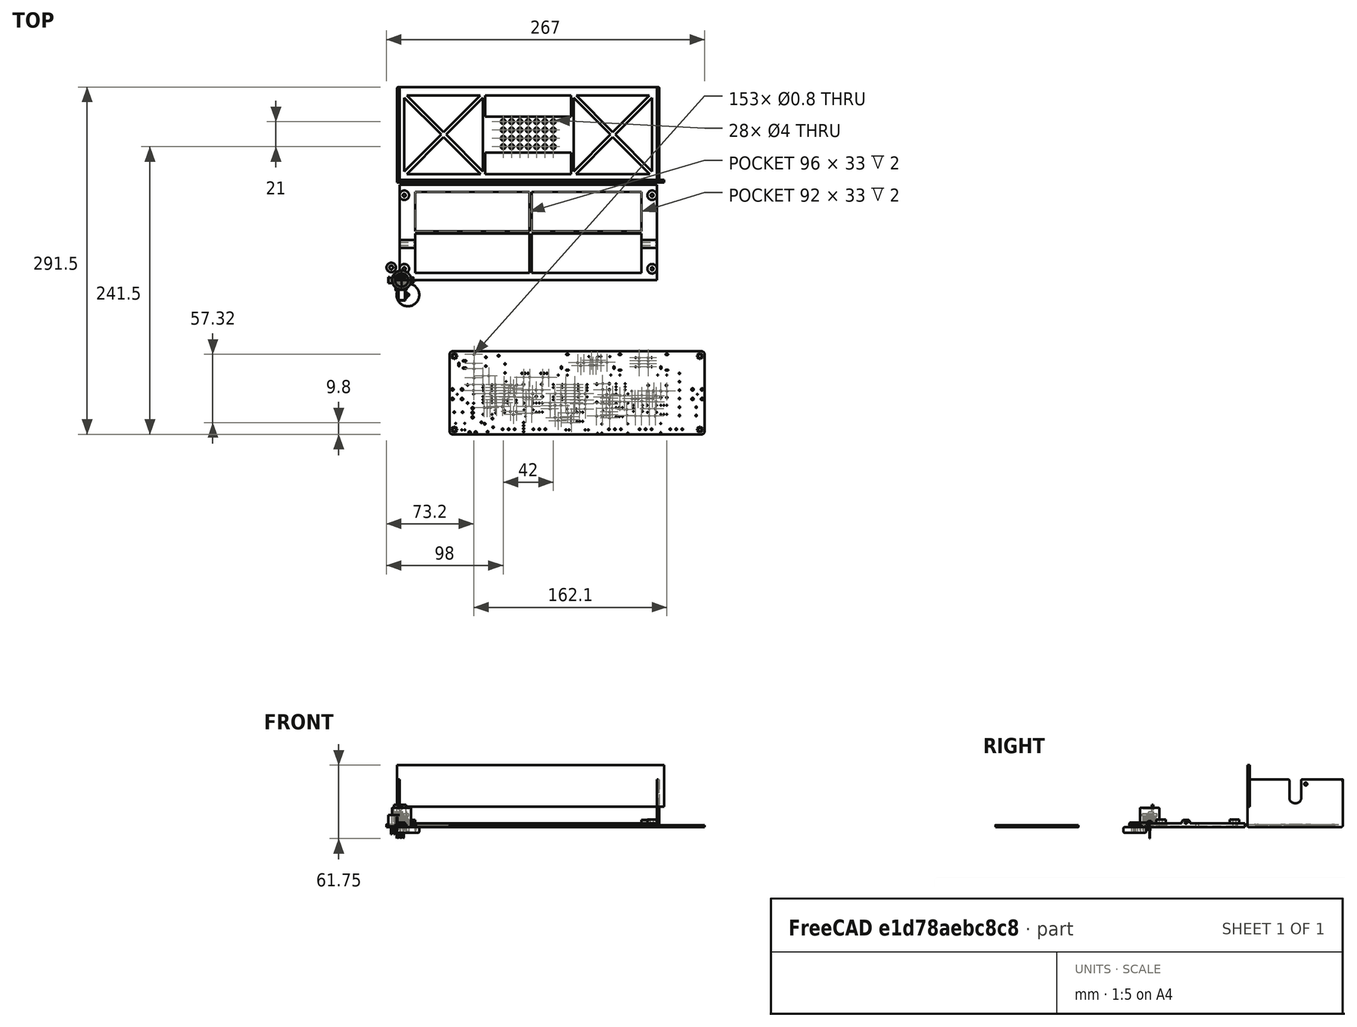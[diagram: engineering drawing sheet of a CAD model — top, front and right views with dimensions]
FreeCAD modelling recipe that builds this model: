
FCSTD DOCUMENT  (FreeCAD 0.18R16110 (Git))
Label: theresynth-case
License: All rights reserved
LicenseURL: http://en.wikipedia.org/wiki/All_rights_reserved
objects: Part::Feature×127, App::Part×126, Part::Cylinder×43, Part::Box×18, Part::MultiFuse×7, Part::Cut×6, Part::Fillet×5, Mesh::Feature×5
note: 206 computed .brp shape members not serialized (recipe doc carries the construction recipe); baked Part::Feature solids carry a one-line shape summary decoded from their .brp

FEATURE [Part::Box] Box  label="Base"
  AttacherType = Attacher::AttachEngine3D
  Height = 3
  Length = 216
  Placement = pos=(2,0,0) rot=(0,0,1;0rad)
  Width = 80
FEATURE [Part::Cylinder] Cylinder  label="ScrewHole"
  Angle = 360
  AttacherType = Attacher::AttachEngine3D
  Height = 7
  Placement = pos=(6,9.5,0) rot=(0,0,1;0rad)
  Radius = 1.25
FEATURE [Part::Feature] Part__Feature  label="SOLID"
  shape: bbox 19.77 x 20.45 x 18 mm, 56 faces (baked)
FEATURE [App::Part] CP_Radial_D16_0mm_P7_50mm  label="CP_Radial_D16.0mm_P7.50mm"
  Group = -> [Part__Feature]
  Origin = -> Origin
  Placement = pos=(74.42,-72.22,1.65) rot=(0,0,1;1.5708rad)
FEATURE [Part::Feature] Part__Feature001  label="SOLID001"
  shape: bbox 19.77 x 20.45 x 18 mm, 56 faces (baked)
FEATURE [App::Part] CP_Radial_D16_0mm_P7_50mm001  label="CP_Radial_D16.0mm_P7.50mm001"
  Group = -> [Part__Feature001]
  Origin = -> Origin001
  Placement = pos=(90.52,-70.42,1.65) rot=(0,0,-1;1.5708rad)
FEATURE [Part::Feature] Part__Feature002  label="SOLID002"
  shape: bbox 8.285 x 1.732 x 4.666 mm, 17 faces (baked)
FEATURE [App::Part] R_Axial_DIN0204_L3_6mm_D1_6mm_P7_62mm_Horizontal  label="R_Axial_DIN0204_L3.6mm_D1.6mm_P7.62mm_Horizontal"
  Group = -> [Part__Feature002]
  Origin = -> Origin002
  Placement = pos=(82.5,-111.57,1.65) rot=(0,0,1;0rad)
FEATURE [Part::Feature] Part__Feature003  label="SOLID003"
  shape: bbox 8.306 x 1.61 x 4.605 mm, 21 faces (baked)
FEATURE [App::Part] D_DO_34_SOD68_P7_62mm_Horizontal  label="D_DO-34_SOD68_P7.62mm_Horizontal"
  Group = -> [Part__Feature003]
  Origin = -> Origin003
  Placement = pos=(90.1,-109.17,1.65) rot=(0,0,1;3.14159rad)
FEATURE [Part::Feature] Part__Feature004  label="SOLID004"
  shape: bbox 8.306 x 1.61 x 4.605 mm, 21 faces (baked)
FEATURE [App::Part] D_DO_34_SOD68_P7_62mm_Horizontal001  label="D_DO-34_SOD68_P7.62mm_Horizontal001"
  Group = -> [Part__Feature004]
  Origin = -> Origin004
  Placement = pos=(64.2,-95.7,1.65) rot=(0,0,-1;1.5708rad)
FEATURE [Part::Feature] Part__Feature005  label="SOLID005"
  shape: bbox 8.306 x 1.61 x 4.605 mm, 21 faces (baked)
FEATURE [App::Part] D_DO_34_SOD68_P7_62mm_Horizontal002  label="D_DO-34_SOD68_P7.62mm_Horizontal002"
  Group = -> [Part__Feature005]
  Origin = -> Origin005
  Placement = pos=(178.49,-64.2,1.65) rot=(0,0,1;3.14159rad)
FEATURE [Part::Feature] Part__Feature006  label="SOLID006"
  shape: bbox 2.54 x 10.16 x 11.54 mm, 100 faces (baked)
FEATURE [App::Part] PinHeader_1x04_P2_54mm_Vertical  label="PinHeader_1x04_P2.54mm_Vertical"
  Group = -> [Part__Feature006]
  Origin = -> Origin006
  Placement = pos=(106.2,-127.27,1.65) rot=(0,0,1;3.14159rad)
FEATURE [Part::Feature] Part__Feature007  label="SOLID007"
  shape: bbox 8.285 x 1.732 x 4.666 mm, 17 faces (baked)
FEATURE [App::Part] R_Axial_DIN0204_L3_6mm_D1_6mm_P7_62mm_Horizontal001  label="R_Axial_DIN0204_L3.6mm_D1.6mm_P7.62mm_Horizontal001"
  Group = -> [Part__Feature007]
  Origin = -> Origin007
  Placement = pos=(221.2,-120.47,1.65) rot=(0,0,-1;1.5708rad)
FEATURE [Part::Feature] Part__Feature008  label="SOLID008"
  shape: bbox 8.285 x 1.732 x 4.666 mm, 17 faces (baked)
FEATURE [App::Part] R_Axial_DIN0204_L3_6mm_D1_6mm_P7_62mm_Horizontal002  label="R_Axial_DIN0204_L3.6mm_D1.6mm_P7.62mm_Horizontal002"
  Group = -> [Part__Feature008]
  Origin = -> Origin008
  Placement = pos=(200.1,-72.77,1.65) rot=(0,0,1;1.5708rad)
FEATURE [Part::Feature] Part__Feature009  label="SOLID009"
  shape: bbox 7.874 x 9.27 x 6.98 mm, 148 faces (baked)
FEATURE [App::Part] DIP_8_W7_62mm  label="DIP-8_W7.62mm"
  Group = -> [Part__Feature009]
  Origin = -> Origin009
  Placement = pos=(203,-65.17,1.65) rot=(0,0,1;0rad)
FEATURE [Part::Feature] Part__Feature010  label="SOLID010"
  shape: bbox 7.874 x 19.05 x 6.98 mm, 250 faces (baked)
FEATURE [App::Part] DIP_14_W7_62mm  label="DIP-14_W7.62mm"
  Group = -> [Part__Feature010]
  Origin = -> Origin010
  Placement = pos=(141.46,-87.66,1.65) rot=(0,0,1;0rad)
FEATURE [Part::Feature] Part__Feature011  label="SOLID011"
  shape: bbox 8.285 x 1.732 x 4.666 mm, 17 faces (baked)
FEATURE [App::Part] R_Axial_DIN0204_L3_6mm_D1_6mm_P7_62mm_Horizontal003  label="R_Axial_DIN0204_L3.6mm_D1.6mm_P7.62mm_Horizontal003"
  Group = -> [Part__Feature011]
  Origin = -> Origin011
  Placement = pos=(72.01,-92.65,1.65) rot=(0,0,1;0rad)
FEATURE [Part::Feature] Part__Feature012  label="SOLID012"
  shape: bbox 7 x 6 x 11.9 mm, 22 faces (baked)
FEATURE [App::Part] C_Rect_L7_0mm_W6_0mm_P5_00mm  label="C_Rect_L7.0mm_W6.0mm_P5.00mm"
  Group = -> [Part__Feature012]
  Origin = -> Origin012
  Placement = pos=(172.3,-114.14,1.65) rot=(0,0,1;3.14159rad)
FEATURE [Part::Feature] Part__Feature013  label="SOLID013"
  shape: bbox 8.285 x 1.732 x 4.666 mm, 17 faces (baked)
FEATURE [App::Part] R_Axial_DIN0204_L3_6mm_D1_6mm_P7_62mm_Horizontal004  label="R_Axial_DIN0204_L3.6mm_D1.6mm_P7.62mm_Horizontal004"
  Group = -> [Part__Feature013]
  Origin = -> Origin013
  Placement = pos=(72.02,-87.86,1.65) rot=(0,0,1;0rad)
FEATURE [Part::Feature] Part__Feature014  label="SOLID014"
  shape: bbox 8.285 x 1.732 x 4.666 mm, 17 faces (baked)
FEATURE [App::Part] R_Axial_DIN0204_L3_6mm_D1_6mm_P7_62mm_Horizontal005  label="R_Axial_DIN0204_L3.6mm_D1.6mm_P7.62mm_Horizontal005"
  Group = -> [Part__Feature014]
  Origin = -> Origin014
  Placement = pos=(79.64,-90.245,1.65) rot=(0,0,1;3.14159rad)
FEATURE [Part::Feature] Part__Feature015  label="SOLID015"
  shape: bbox 8.285 x 1.732 x 4.666 mm, 17 faces (baked)
FEATURE [App::Part] R_Axial_DIN0204_L3_6mm_D1_6mm_P7_62mm_Horizontal006  label="R_Axial_DIN0204_L3.6mm_D1.6mm_P7.62mm_Horizontal006"
  Group = -> [Part__Feature015]
  Origin = -> Origin015
  Placement = pos=(193.68,-103.2,1.65) rot=(0,0,1;1.5708rad)
FEATURE [Part::Feature] Part__Feature016  label="SOLID016"
  shape: bbox 6 x 2.5 x 8.1 mm, 12 faces (baked)
FEATURE [App::Part] C_Disc_D6_0mm_W2_5mm_P5_00mm  label="C_Disc_D6.0mm_W2.5mm_P5.00mm"
  Group = -> [Part__Feature016]
  Origin = -> Origin016
  Placement = pos=(172.4,-91.94,1.65) rot=(0,0,1;1.5708rad)
FEATURE [Part::Feature] Part__Feature017  label="SOLID017"
  shape: bbox 7.874 x 19.05 x 6.98 mm, 250 faces (baked)
FEATURE [App::Part] DIP_14_W7_62mm001  label="DIP-14_W7.62mm001"
  Group = -> [Part__Feature017]
  Origin = -> Origin017
  Placement = pos=(82.21,-87.7,1.65) rot=(0,0,1;0rad)
FEATURE [Part::Feature] Part__Feature018  label="SOLID018"
  shape: bbox 8.285 x 1.732 x 4.666 mm, 17 faces (baked)
FEATURE [App::Part] R_Axial_DIN0204_L3_6mm_D1_6mm_P7_62mm_Horizontal007  label="R_Axial_DIN0204_L3.6mm_D1.6mm_P7.62mm_Horizontal007"
  Group = -> [Part__Feature018]
  Origin = -> Origin018
  Placement = pos=(72,-112.77,1.65) rot=(0,0,1;0rad)
FEATURE [Part::Feature] Part__Feature019  label="SOLID019"
  shape: bbox 10.25 x 4.455 x 28.53 mm, 48 faces (baked)
FEATURE [App::Part] TO_220_3_Vertical  label="TO-220-3_Vertical"
  Group = -> [Part__Feature019]
  Origin = -> Origin019
  Placement = pos=(104.83,-78.28,1.65) rot=(0,0,1;0rad)
FEATURE [Part::Feature] Part__Feature020  label="SOLID020"
  shape: bbox 10.25 x 4.455 x 28.53 mm, 48 faces (baked)
FEATURE [App::Part] TO_220_3_Vertical001  label="TO-220-3_Vertical001"
  Group = -> [Part__Feature020]
  Origin = -> Origin020
  Placement = pos=(120.77,-78.28,1.65) rot=(0,0,1;0rad)
FEATURE [Part::Feature] Part__Feature021  label="SOLID021"
  shape: bbox 2.8 x 0.6 x 8.5 mm, 15 faces (baked)
FEATURE [App::Part] Pin_D1_4mm_L8_5mm_W2_8mm_FlatFork  label="Pin_D1.4mm_L8.5mm_W2.8mm_FlatFork"
  Group = -> [Part__Feature021]
  Origin = -> Origin021
  Placement = pos=(85.16,-63.49,1.65) rot=(0,0,1;0rad)
FEATURE [Part::Feature] Part__Feature022  label="SOLID022"
  shape: bbox 8.285 x 1.732 x 4.666 mm, 17 faces (baked)
FEATURE [App::Part] R_Axial_DIN0204_L3_6mm_D1_6mm_P7_62mm_Horizontal008  label="R_Axial_DIN0204_L3.6mm_D1.6mm_P7.62mm_Horizontal008"
  Group = -> [Part__Feature022]
  Origin = -> Origin022
  Placement = pos=(56.7,-120.2,1.65) rot=(0,0,1;3.14159rad)
FEATURE [Part::Feature] Part__Feature023  label="SOLID023"
  shape: bbox 3.4 x 3.8 x 10.8 mm, 16 faces (baked)
FEATURE [App::Part] LED_D3_0mm  label="LED_D3.0mm"
  Group = -> [Part__Feature023]
  Origin = -> Origin023
  Placement = pos=(54.2,-125.75,1.65) rot=(0,0,1;0rad)
FEATURE [Part::Feature] Part__Feature024  label="SOLID024"
  shape: bbox 8.285 x 1.732 x 4.666 mm, 17 faces (baked)
FEATURE [App::Part] R_Axial_DIN0204_L3_6mm_D1_6mm_P7_62mm_Horizontal009  label="R_Axial_DIN0204_L3.6mm_D1.6mm_P7.62mm_Horizontal009"
  Group = -> [Part__Feature024]
  Origin = -> Origin024
  Placement = pos=(138.72,-87.64,1.65) rot=(0,0,1;3.14159rad)
FEATURE [Part::Feature] Part__Feature025  label="SOLID025"
  shape: bbox 8.285 x 1.732 x 4.666 mm, 17 faces (baked)
FEATURE [App::Part] R_Axial_DIN0204_L3_6mm_D1_6mm_P7_62mm_Horizontal010  label="R_Axial_DIN0204_L3.6mm_D1.6mm_P7.62mm_Horizontal010"
  Group = -> [Part__Feature025]
  Origin = -> Origin025
  Placement = pos=(159.43,-87.72,1.65) rot=(0,0,1;3.14159rad)
FEATURE [Part::Feature] Part__Feature026  label="SOLID026"
  shape: bbox 9.53 x 4.83 x 17.07 mm, 32 faces (baked)
FEATURE [App::Part] Potentiometer_Bourns_3296W_Vertical
  Group = -> [Part__Feature026]
  Origin = -> Origin026
  Placement = pos=(161.84,-71.6,1.65) rot=(0,0,1;3.14159rad)
FEATURE [Part::Feature] Part__Feature027  label="SOLID027"
  shape: bbox 8.285 x 1.732 x 4.666 mm, 17 faces (baked)
FEATURE [App::Part] R_Axial_DIN0204_L3_6mm_D1_6mm_P7_62mm_Horizontal011  label="R_Axial_DIN0204_L3.6mm_D1.6mm_P7.62mm_Horizontal011"
  Group = -> [Part__Feature027]
  Origin = -> Origin027
  Placement = pos=(213.6,-72.77,1.65) rot=(0,0,1;1.5708rad)
FEATURE [Part::Feature] Part__Feature028  label="SOLID028"
  shape: bbox 3.4 x 3.8 x 10.8 mm, 16 faces (baked)
FEATURE [App::Part] LED_D3_0mm001  label="LED_D3.0mm001"
  Group = -> [Part__Feature028]
  Origin = -> Origin028
  Placement = pos=(157.84,-125.75,1.65) rot=(0,0,1;0rad)
FEATURE [Part::Feature] Part__Feature029  label="SOLID029"
  shape: bbox 9.53 x 4.83 x 17.07 mm, 32 faces (baked)
FEATURE [App::Part] Potentiometer_Bourns_3296W_Vertical001
  Group = -> [Part__Feature029]
  Origin = -> Origin029
  Placement = pos=(78.1,-107,1.65) rot=(0,0,1;0rad)
FEATURE [Part::Feature] Part__Feature030  label="SOLID030"
  shape: bbox 7.2 x 2.5 x 10.9 mm, 22 faces (baked)
FEATURE [App::Part] C_Rect_L7_2mm_W2_5mm_P5_00mm_FKS2_FKP2_MKS2_MKP2  label="C_Rect_L7.2mm_W2.5mm_P5.00mm_FKS2_FKP2_MKS2_MKP2"
  Group = -> [Part__Feature030]
  Origin = -> Origin030
  Placement = pos=(93.6,-94.9,1.65) rot=(0,0,1;0rad)
FEATURE [Part::Feature] Part__Feature031  label="SOLID031"
  shape: bbox 7.2 x 2.5 x 10.9 mm, 22 faces (baked)
FEATURE [App::Part] C_Rect_L7_2mm_W2_5mm_P5_00mm_FKS2_FKP2_MKS2_MKP2001  label="C_Rect_L7.2mm_W2.5mm_P5.00mm_FKS2_FKP2_MKS2_MKP003"
  Group = -> [Part__Feature031]
  Origin = -> Origin031
  Placement = pos=(78.2,-95.3,1.65) rot=(0,0,1;3.14159rad)
FEATURE [Part::Feature] Part__Feature032  label="SOLID032"
  shape: bbox 7.2 x 2.5 x 10.9 mm, 22 faces (baked)
FEATURE [App::Part] C_Rect_L7_2mm_W2_5mm_P5_00mm_FKS2_FKP2_MKS2_MKP2002  label="C_Rect_L7.2mm_W2.5mm_P5.00mm_FKS2_FKP2_MKS2_MKP004"
  Group = -> [Part__Feature032]
  Origin = -> Origin032
  Placement = pos=(152.9,-95.4,1.65) rot=(0,0,1;0rad)
FEATURE [Part::Feature] Part__Feature033  label="SOLID033"
  shape: bbox 7.2 x 2.5 x 10.9 mm, 22 faces (baked)
FEATURE [App::Part] C_Rect_L7_2mm_W2_5mm_P5_00mm_FKS2_FKP2_MKS2_MKP2003  label="C_Rect_L7.2mm_W2.5mm_P5.00mm_FKS2_FKP2_MKS2_MKP005"
  Group = -> [Part__Feature033]
  Origin = -> Origin033
  Placement = pos=(137.4,-95.3,1.65) rot=(0,0,1;3.14159rad)
FEATURE [Part::Feature] Part__Feature034  label="SOLID034"
  shape: bbox 7.2 x 2.5 x 10.9 mm, 22 faces (baked)
FEATURE [App::Part] C_Rect_L7_2mm_W2_5mm_P5_00mm_FKS2_FKP2_MKS2_MKP2004  label="C_Rect_L7.2mm_W2.5mm_P5.00mm_FKS2_FKP2_MKS2_MKP006"
  Group = -> [Part__Feature034]
  Origin = -> Origin034
  Placement = pos=(180.9,-96.1,1.65) rot=(0,0,1;3.14159rad)
FEATURE [Part::Feature] Part__Feature035  label="SOLID035"
  shape: bbox 7.2 x 2.5 x 10.9 mm, 22 faces (baked)
FEATURE [App::Part] C_Rect_L7_2mm_W2_5mm_P5_00mm_FKS2_FKP2_MKS2_MKP2005  label="C_Rect_L7.2mm_W2.5mm_P5.00mm_FKS2_FKP2_MKS2_MKP007"
  Group = -> [Part__Feature035]
  Origin = -> Origin035
  Placement = pos=(217.2,-102.1,1.65) rot=(0,0,1;1.5708rad)
FEATURE [Part::Feature] Part__Feature036  label="COMPOUND"
  shape: bbox 8.244 x 2.165 x 5.082 mm, 16 faces, 2 solids (baked)
FEATURE [App::Part] D_DO_35_SOD27_P7_62mm_Horizontal  label="D_DO-35_SOD27_P7.62mm_Horizontal"
  Group = -> [Part__Feature036]
  Origin = -> Origin036
  Placement = pos=(64.5,-70,1.65) rot=(0,0,1;1.5708rad)
FEATURE [Part::Feature] Part__Feature037  label="COMPOUND001"
  shape: bbox 8.244 x 2.165 x 5.082 mm, 16 faces, 2 solids (baked)
FEATURE [App::Part] D_DO_35_SOD27_P7_62mm_Horizontal001  label="D_DO-35_SOD27_P7.62mm_Horizontal001"
  Group = -> [Part__Feature037]
  Origin = -> Origin037
  Placement = pos=(64.45,-82.05,1.65) rot=(0,0,1;1.5708rad)
FEATURE [Part::Feature] Part__Feature038  label="SOLID036"
  shape: bbox 8.285 x 1.732 x 4.666 mm, 17 faces (baked)
FEATURE [App::Part] R_Axial_DIN0204_L3_6mm_D1_6mm_P7_62mm_Horizontal012  label="R_Axial_DIN0204_L3.6mm_D1.6mm_P7.62mm_Horizontal012"
  Group = -> [Part__Feature038]
  Origin = -> Origin038
  Placement = pos=(92.4,-100.75,1.65) rot=(0,0,1;0rad)
FEATURE [Part::Feature] Part__Feature039  label="SOLID037"
  shape: bbox 8.285 x 1.732 x 4.666 mm, 17 faces (baked)
FEATURE [App::Part] R_Axial_DIN0204_L3_6mm_D1_6mm_P7_62mm_Horizontal013  label="R_Axial_DIN0204_L3.6mm_D1.6mm_P7.62mm_Horizontal013"
  Group = -> [Part__Feature039]
  Origin = -> Origin039
  Placement = pos=(226.3,-79.77,1.65) rot=(0,0,1;3.14159rad)
FEATURE [Part::Feature] Part__Feature040  label="SOLID038"
  shape: bbox 8.285 x 1.732 x 4.666 mm, 17 faces (baked)
FEATURE [App::Part] R_Axial_DIN0204_L3_6mm_D1_6mm_P7_62mm_Horizontal014  label="R_Axial_DIN0204_L3.6mm_D1.6mm_P7.62mm_Horizontal014"
  Group = -> [Part__Feature040]
  Origin = -> Origin040
  Placement = pos=(186.94,-79.77,1.65) rot=(0,0,1;3.14159rad)
FEATURE [Part::Feature] Part__Feature041  label="SOLID039"
  shape: bbox 8.285 x 1.732 x 4.666 mm, 17 faces (baked)
FEATURE [App::Part] R_Axial_DIN0204_L3_6mm_D1_6mm_P7_62mm_Horizontal015  label="R_Axial_DIN0204_L3.6mm_D1.6mm_P7.62mm_Horizontal015"
  Group = -> [Part__Feature041]
  Origin = -> Origin041
  Placement = pos=(151.79,-90.22,1.65) rot=(0,0,1;0rad)
FEATURE [Part::Feature] Part__Feature042  label="SOLID040"
  shape: bbox 8.285 x 1.732 x 4.666 mm, 17 faces (baked)
FEATURE [App::Part] R_Axial_DIN0204_L3_6mm_D1_6mm_P7_62mm_Horizontal016  label="R_Axial_DIN0204_L3.6mm_D1.6mm_P7.62mm_Horizontal016"
  Group = -> [Part__Feature042]
  Origin = -> Origin042
  Placement = pos=(151.8,-98.1,1.65) rot=(0,0,1;0rad)
FEATURE [Part::Feature] Part__Feature043  label="SOLID041"
  shape: bbox 8.285 x 1.732 x 4.666 mm, 17 faces (baked)
FEATURE [App::Part] R_Axial_DIN0204_L3_6mm_D1_6mm_P7_62mm_Horizontal017  label="R_Axial_DIN0204_L3.6mm_D1.6mm_P7.62mm_Horizontal017"
  Group = -> [Part__Feature043]
  Origin = -> Origin043
  Placement = pos=(168.49,-64.2,1.65) rot=(0,0,1;3.14159rad)
FEATURE [Part::Feature] Part__Feature044  label="SOLID042"
  shape: bbox 8.285 x 1.732 x 4.666 mm, 17 faces (baked)
FEATURE [App::Part] R_Axial_DIN0204_L3_6mm_D1_6mm_P7_62mm_Horizontal018  label="R_Axial_DIN0204_L3.6mm_D1.6mm_P7.62mm_Horizontal018"
  Group = -> [Part__Feature044]
  Origin = -> Origin044
  Placement = pos=(159.4,-92.7,1.65) rot=(0,0,1;3.14159rad)
FEATURE [Part::Feature] Part__Feature045  label="SOLID043"
  shape: bbox 7.2 x 2.5 x 10.9 mm, 22 faces (baked)
FEATURE [App::Part] C_Rect_L7_2mm_W2_5mm_P5_00mm_FKS2_FKP2_MKS2_MKP2006  label="C_Rect_L7.2mm_W2.5mm_P5.00mm_FKS2_FKP2_MKS2_MKP008"
  Group = -> [Part__Feature045]
  Origin = -> Origin045
  Placement = pos=(152.9,-103.9,1.65) rot=(0,0,1;0rad)
FEATURE [Part::Feature] Part__Feature046  label="SOLID044"
  shape: bbox 7 x 6 x 11.9 mm, 22 faces (baked)
FEATURE [App::Part] C_Rect_L7_0mm_W6_0mm_P5_00mm001  label="C_Rect_L7.0mm_W6.0mm_P5.00mm001"
  Group = -> [Part__Feature046]
  Origin = -> Origin046
  Placement = pos=(176.09,-69,1.65) rot=(0,0,1;3.14159rad)
FEATURE [Part::Feature] Part__Feature047  label="SOLID045"
  shape: bbox 7.2 x 2.5 x 10.9 mm, 22 faces (baked)
FEATURE [App::Part] C_Rect_L7_2mm_W2_5mm_P5_00mm_FKS2_FKP2_MKS2_MKP2007  label="C_Rect_L7.2mm_W2.5mm_P5.00mm_FKS2_FKP2_MKS2_MKP009"
  Group = -> [Part__Feature047]
  Origin = -> Origin047
  Placement = pos=(152.9,-100.8,1.65) rot=(0,0,1;0rad)
FEATURE [Part::Feature] Part__Feature048  label="SOLID046"
  shape: bbox 7.2 x 2.5 x 10.9 mm, 22 faces (baked)
FEATURE [App::Part] C_Rect_L7_2mm_W2_5mm_P5_00mm_FKS2_FKP2_MKS2_MKP2008  label="C_Rect_L7.2mm_W2.5mm_P5.00mm_FKS2_FKP2_MKS2_MKP010"
  Group = -> [Part__Feature048]
  Origin = -> Origin048
  Placement = pos=(168.07,-67.22,1.65) rot=(0,0,1;3.14159rad)
FEATURE [Part::Feature] Part__Feature049  label="SOLID047"
  shape: bbox 5.58 x 3.745 x 10 mm, 27 faces (baked)
FEATURE [App::Part] TO_92_Inline_Wide  label="TO-92_Inline_Wide"
  Group = -> [Part__Feature049]
  Origin = -> Origin049
  Placement = pos=(105.7,-98.4,1.65) rot=(0,0,1;0rad)
FEATURE [Part::Feature] Part__Feature050  label="SOLID048"
  shape: bbox 5.58 x 3.745 x 10 mm, 27 faces (baked)
FEATURE [App::Part] TO_92_Inline_Wide001  label="TO-92_Inline_Wide001"
  Group = -> [Part__Feature050]
  Origin = -> Origin050
  Placement = pos=(128.4,-108.1,1.65) rot=(0,0,1;1.5708rad)
FEATURE [Part::Feature] Part__Feature051  label="SOLID049"
  shape: bbox 5.58 x 3.745 x 10 mm, 27 faces (baked)
FEATURE [App::Part] TO_92_Inline_Wide002  label="TO-92_Inline_Wide002"
  Group = -> [Part__Feature051]
  Origin = -> Origin051
  Placement = pos=(146.1,-119.7,1.65) rot=(0,0,1;1.5708rad)
FEATURE [Part::Feature] Part__Feature052  label="SOLID050"
  shape: bbox 5.58 x 3.745 x 10 mm, 27 faces (baked)
FEATURE [App::Part] TO_92_Inline_Wide003  label="TO-92_Inline_Wide003"
  Group = -> [Part__Feature052]
  Origin = -> Origin052
  Placement = pos=(178.3,-115.7,1.65) rot=(0,0,1;1.5708rad)
FEATURE [Part::Feature] Part__Feature053  label="SOLID051"
  shape: bbox 5.58 x 3.745 x 10 mm, 27 faces (baked)
FEATURE [App::Part] TO_92_Inline_Wide004  label="TO-92_Inline_Wide004"
  Group = -> [Part__Feature053]
  Origin = -> Origin053
  Placement = pos=(197.1,-99.5,1.65) rot=(0,0,1;0rad)
FEATURE [Part::Feature] Part__Feature054  label="SOLID052"
  shape: bbox 5.58 x 3.745 x 10 mm, 27 faces (baked)
FEATURE [App::Part] TO_92_Inline_Wide005  label="TO-92_Inline_Wide005"
  Group = -> [Part__Feature054]
  Origin = -> Origin054
  Placement = pos=(178.2,-104.2,1.65) rot=(0,0,1;1.5708rad)
FEATURE [Part::Feature] Part__Feature055  label="SOLID053"
  shape: bbox 5.58 x 3.745 x 10 mm, 27 faces (baked)
FEATURE [App::Part] TO_92_Inline_Wide006  label="TO-92_Inline_Wide006"
  Group = -> [Part__Feature055]
  Origin = -> Origin055
  Placement = pos=(209.1,-99.2,1.65) rot=(0,0,1;0rad)
FEATURE [Part::Feature] Part__Feature056  label="SOLID054"
  shape: bbox 3.4 x 3.8 x 10.8 mm, 16 faces (baked)
FEATURE [App::Part] LED_D3_0mm002  label="LED_D3.0mm002"
  Group = -> [Part__Feature056]
  Origin = -> Origin056
  Placement = pos=(141.6,-125.75,1.65) rot=(0,0,1;0rad)
FEATURE [Part::Feature] Part__Feature057  label="SOLID055"
  shape: bbox 8.285 x 1.732 x 4.666 mm, 17 faces (baked)
FEATURE [App::Part] R_Axial_DIN0204_L3_6mm_D1_6mm_P7_62mm_Horizontal019  label="R_Axial_DIN0204_L3.6mm_D1.6mm_P7.62mm_Horizontal019"
  Group = -> [Part__Feature057]
  Origin = -> Origin057
  Placement = pos=(142.83,-79.77,1.65) rot=(0,0,1;3.14159rad)
FEATURE [Part::Feature] Part__Feature058  label="SOLID056"
  shape: bbox 8.285 x 1.732 x 4.666 mm, 17 faces (baked)
FEATURE [App::Part] R_Axial_DIN0204_L3_6mm_D1_6mm_P7_62mm_Horizontal020  label="R_Axial_DIN0204_L3.6mm_D1.6mm_P7.62mm_Horizontal020"
  Group = -> [Part__Feature058]
  Origin = -> Origin058
  Placement = pos=(72,-102.9,1.65) rot=(0,0,1;0rad)
FEATURE [Part::Feature] Part__Feature059  label="SOLID057"
  shape: bbox 8.285 x 1.732 x 4.666 mm, 17 faces (baked)
FEATURE [App::Part] R_Axial_DIN0204_L3_6mm_D1_6mm_P7_62mm_Horizontal021  label="R_Axial_DIN0204_L3.6mm_D1.6mm_P7.62mm_Horizontal021"
  Group = -> [Part__Feature059]
  Origin = -> Origin059
  Placement = pos=(72,-100.4,1.65) rot=(0,0,1;0rad)
FEATURE [Part::Feature] Part__Feature060  label="SOLID058"
  shape: bbox 8.285 x 1.732 x 4.666 mm, 17 faces (baked)
FEATURE [App::Part] R_Axial_DIN0204_L3_6mm_D1_6mm_P7_62mm_Horizontal022  label="R_Axial_DIN0204_L3.6mm_D1.6mm_P7.62mm_Horizontal022"
  Group = -> [Part__Feature060]
  Origin = -> Origin060
  Placement = pos=(79.6,-97.9,1.65) rot=(0,0,1;3.14159rad)
FEATURE [Part::Feature] Part__Feature061  label="SOLID059"
  shape: bbox 8.285 x 1.732 x 4.666 mm, 17 faces (baked)
FEATURE [App::Part] R_Axial_DIN0204_L3_6mm_D1_6mm_P7_62mm_Horizontal023  label="R_Axial_DIN0204_L3.6mm_D1.6mm_P7.62mm_Horizontal023"
  Group = -> [Part__Feature061]
  Origin = -> Origin061
  Placement = pos=(100.1,-103.1,1.65) rot=(0,0,1;3.14159rad)
FEATURE [Part::Feature] Part__Feature062  label="SOLID060"
  shape: bbox 8.285 x 1.732 x 4.666 mm, 17 faces (baked)
FEATURE [App::Part] R_Axial_DIN0204_L3_6mm_D1_6mm_P7_62mm_Horizontal024  label="R_Axial_DIN0204_L3.6mm_D1.6mm_P7.62mm_Horizontal024"
  Group = -> [Part__Feature062]
  Origin = -> Origin062
  Placement = pos=(106.6,-103.3,1.65) rot=(0,0,1;0rad)
FEATURE [Part::Feature] Part__Feature063  label="SOLID061"
  shape: bbox 8.285 x 1.732 x 4.666 mm, 17 faces (baked)
FEATURE [App::Part] R_Axial_DIN0204_L3_6mm_D1_6mm_P7_62mm_Horizontal025  label="R_Axial_DIN0204_L3.6mm_D1.6mm_P7.62mm_Horizontal025"
  Group = -> [Part__Feature063]
  Origin = -> Origin063
  Placement = pos=(121.9,-110.8,1.65) rot=(0,0,1;1.5708rad)
FEATURE [Part::Feature] Part__Feature064  label="SOLID062"
  shape: bbox 8.285 x 1.732 x 4.666 mm, 17 faces (baked)
FEATURE [App::Part] R_Axial_DIN0204_L3_6mm_D1_6mm_P7_62mm_Horizontal026  label="R_Axial_DIN0204_L3.6mm_D1.6mm_P7.62mm_Horizontal026"
  Group = -> [Part__Feature064]
  Origin = -> Origin064
  Placement = pos=(106.6,-108.9,1.65) rot=(0,0,1;0rad)
FEATURE [Part::Feature] Part__Feature065  label="SOLID063"
  shape: bbox 8.285 x 1.732 x 4.666 mm, 17 faces (baked)
FEATURE [App::Part] R_Axial_DIN0204_L3_6mm_D1_6mm_P7_62mm_Horizontal027  label="R_Axial_DIN0204_L3.6mm_D1.6mm_P7.62mm_Horizontal027"
  Group = -> [Part__Feature065]
  Origin = -> Origin065
  Placement = pos=(119.3,-110.8,1.65) rot=(0,0,1;1.5708rad)
FEATURE [Part::Feature] Part__Feature066  label="SOLID064"
  shape: bbox 8.285 x 1.732 x 4.666 mm, 17 faces (baked)
FEATURE [App::Part] R_Axial_DIN0204_L3_6mm_D1_6mm_P7_62mm_Horizontal028  label="R_Axial_DIN0204_L3.6mm_D1.6mm_P7.62mm_Horizontal028"
  Group = -> [Part__Feature066]
  Origin = -> Origin066
  Placement = pos=(116.7,-103.2,1.65) rot=(0,0,-1;1.5708rad)
FEATURE [Part::Feature] Part__Feature067  label="SOLID065"
  shape: bbox 12.5 x 12.5 x 13.85 mm, 27 faces (baked)
FEATURE [App::Part] L_Radial_D12_5mm_P7_00mm_Fastron_09HCP  label="L_Radial_D12.5mm_P7.00mm_Fastron_09HCP"
  Group = -> [Part__Feature067]
  Origin = -> Origin067
  Placement = pos=(47.9,-110.9,1.65) rot=(0,0,1;0rad)
FEATURE [Part::Feature] Part__Feature068  label="SOLID066"
  shape: bbox 16.36 x 5 x 8.1 mm, 35 faces (baked)
FEATURE [App::Part] L_Axial_L12_0mm_D5_0mm_P15_24mm_Horizontal_Fastron_MISC  label="L_Axial_L12.0mm_D5.0mm_P15.24mm_Horizontal_Fastron_MISC"
  Group = -> [Part__Feature068]
  Origin = -> Origin068
  Placement = pos=(59.1,-103.3,1.65) rot=(0,0,1;1.5708rad)
FEATURE [Part::Feature] Part__Feature069  label="SOLID067"
  shape: bbox 16.36 x 5 x 8.1 mm, 35 faces (baked)
FEATURE [App::Part] L_Axial_L12_0mm_D5_0mm_P15_24mm_Horizontal_Fastron_MISC001  label="L_Axial_L12.0mm_D5.0mm_P15.24mm_Horizontal_Fastron_MISC001"
  Group = -> [Part__Feature069]
  Origin = -> Origin069
  Placement = pos=(106,-87.5,1.65) rot=(0,0,1;0rad)
FEATURE [Part::Feature] Part__Feature070  label="SOLID068"
  shape: bbox 7.2 x 2.5 x 10.9 mm, 22 faces (baked)
FEATURE [App::Part] C_Rect_L7_2mm_W2_5mm_P5_00mm_FKS2_FKP2_MKS2_MKP2009  label="C_Rect_L7.2mm_W2.5mm_P5.00mm_FKS2_FKP2_MKS2_MKP011"
  Group = -> [Part__Feature070]
  Origin = -> Origin070
  Placement = pos=(93.6,-98,1.65) rot=(0,0,1;0rad)
FEATURE [Part::Feature] Part__Feature071  label="SOLID069"
  shape: bbox 7.2 x 2.5 x 10.9 mm, 22 faces (baked)
FEATURE [App::Part] C_Rect_L7_2mm_W2_5mm_P5_00mm_FKS2_FKP2_MKS2_MKP2010  label="C_Rect_L7.2mm_W2.5mm_P5.00mm_FKS2_FKP2_MKS2_MKP012"
  Group = -> [Part__Feature071]
  Origin = -> Origin071
  Placement = pos=(83.3,-106.2,1.65) rot=(0,0,1;0rad)
FEATURE [Part::Feature] Part__Feature072  label="SOLID070"
  shape: bbox 6 x 2.5 x 8.1 mm, 12 faces (baked)
FEATURE [App::Part] C_Disc_D6_0mm_W2_5mm_P5_00mm001  label="C_Disc_D6.0mm_W2.5mm_P5.00mm001"
  Group = -> [Part__Feature072]
  Origin = -> Origin072
  Placement = pos=(64.2,-87.7,1.65) rot=(0,0,-1;1.5708rad)
FEATURE [Part::Feature] Part__Feature073  label="SOLID071"
  shape: bbox 7.2 x 2.5 x 10.9 mm, 22 faces (baked)
FEATURE [App::Part] C_Rect_L7_2mm_W2_5mm_P5_00mm_FKS2_FKP2_MKS2_MKP2011  label="C_Rect_L7.2mm_W2.5mm_P5.00mm_FKS2_FKP2_MKS2_MKP013"
  Group = -> [Part__Feature073]
  Origin = -> Origin073
  Placement = pos=(113.7,-100.4,1.65) rot=(0,0,1;1.5708rad)
FEATURE [Part::Feature] Part__Feature074  label="SOLID072"
  shape: bbox 7.2 x 2.5 x 10.9 mm, 22 faces (baked)
FEATURE [App::Part] C_Rect_L7_2mm_W2_5mm_P5_00mm_FKS2_FKP2_MKS2_MKP2012  label="C_Rect_L7.2mm_W2.5mm_P5.00mm_FKS2_FKP2_MKS2_MKP014"
  Group = -> [Part__Feature074]
  Origin = -> Origin074
  Placement = pos=(108,-111.7,1.65) rot=(0,0,1;0rad)
FEATURE [Part::Feature] Part__Feature075  label="SOLID073"
  shape: bbox 7.2 x 2.5 x 10.9 mm, 22 faces (baked)
FEATURE [App::Part] C_Rect_L7_2mm_W2_5mm_P5_00mm_FKS2_FKP2_MKS2_MKP2013  label="C_Rect_L7.2mm_W2.5mm_P5.00mm_FKS2_FKP2_MKS2_MKP015"
  Group = -> [Part__Feature075]
  Origin = -> Origin075
  Placement = pos=(108,-106.1,1.65) rot=(0,0,1;0rad)
FEATURE [Part::Feature] Part__Feature076  label="SOLID074"
  shape: bbox 6 x 2.5 x 8.1 mm, 12 faces (baked)
FEATURE [App::Part] C_Disc_D6_0mm_W2_5mm_P5_00mm002  label="C_Disc_D6.0mm_W2.5mm_P5.00mm002"
  Group = -> [Part__Feature076]
  Origin = -> Origin076
  Placement = pos=(105.6,-92.2,1.65) rot=(0,0,1;0rad)
FEATURE [Part::Feature] Part__Feature077  label="SOLID075"
  shape: bbox 6 x 2.5 x 8.1 mm, 12 faces (baked)
FEATURE [App::Part] C_Disc_D6_0mm_W2_5mm_P5_00mm003  label="C_Disc_D6.0mm_W2.5mm_P5.00mm003"
  Group = -> [Part__Feature077]
  Origin = -> Origin077
  Placement = pos=(116.6,-92.2,1.65) rot=(0,0,1;0rad)
FEATURE [Part::Feature] Part__Feature078  label="SOLID076"
  shape: bbox 7 x 6 x 11.9 mm, 22 faces (baked)
FEATURE [App::Part] C_Rect_L7_0mm_W6_0mm_P5_00mm002  label="C_Rect_L7.0mm_W6.0mm_P5.00mm002"
  Group = -> [Part__Feature078]
  Origin = -> Origin078
  Placement = pos=(71.96,-80.38,1.65) rot=(0,0,1;0rad)
FEATURE [Part::Feature] Part__Feature079  label="SOLID077"
  shape: bbox 7.2 x 2.5 x 10.9 mm, 22 faces (baked)
FEATURE [App::Part] C_Rect_L7_2mm_W2_5mm_P5_00mm_FKS2_FKP2_MKS2_MKP2014  label="C_Rect_L7.2mm_W2.5mm_P5.00mm_FKS2_FKP2_MKS2_MKP016"
  Group = -> [Part__Feature079]
  Origin = -> Origin079
  Placement = pos=(106.25,-81.59,1.65) rot=(0,0,1;0rad)
FEATURE [Part::Feature] Part__Feature080  label="SOLID078"
  shape: bbox 7.2 x 2.5 x 10.9 mm, 22 faces (baked)
FEATURE [App::Part] C_Rect_L7_2mm_W2_5mm_P5_00mm_FKS2_FKP2_MKS2_MKP2015  label="C_Rect_L7.2mm_W2.5mm_P5.00mm_FKS2_FKP2_MKS2_MKP017"
  Group = -> [Part__Feature080]
  Origin = -> Origin080
  Placement = pos=(127.2,-81.62,1.65) rot=(0,0,1;3.14159rad)
FEATURE [Part::Feature] Part__Feature081  label="SOLID079"
  shape: bbox 7 x 6 x 11.9 mm, 22 faces (baked)
FEATURE [App::Part] C_Rect_L7_0mm_W6_0mm_P5_00mm003  label="C_Rect_L7.0mm_W6.0mm_P5.00mm003"
  Group = -> [Part__Feature081]
  Origin = -> Origin081
  Placement = pos=(137.4,-105.3,1.65) rot=(0,0,1;3.14159rad)
FEATURE [Part::Feature] Part__Feature082  label="SOLID080"
  shape: bbox 8.285 x 1.732 x 4.666 mm, 17 faces (baked)
FEATURE [App::Part] R_Axial_DIN0204_L3_6mm_D1_6mm_P7_62mm_Horizontal029  label="R_Axial_DIN0204_L3.6mm_D1.6mm_P7.62mm_Horizontal029"
  Group = -> [Part__Feature082]
  Origin = -> Origin082
  Placement = pos=(138.6,-98.1,1.65) rot=(0,0,1;3.14159rad)
FEATURE [Part::Feature] Part__Feature083  label="SOLID081"
  shape: bbox 8.285 x 1.732 x 4.666 mm, 17 faces (baked)
FEATURE [App::Part] R_Axial_DIN0204_L3_6mm_D1_6mm_P7_62mm_Horizontal030  label="R_Axial_DIN0204_L3.6mm_D1.6mm_P7.62mm_Horizontal030"
  Group = -> [Part__Feature083]
  Origin = -> Origin083
  Placement = pos=(138.6,-100.47,1.65) rot=(0,0,1;3.14159rad)
FEATURE [Part::Feature] Part__Feature084  label="SOLID082"
  shape: bbox 8.285 x 1.732 x 4.666 mm, 17 faces (baked)
FEATURE [App::Part] R_Axial_DIN0204_L3_6mm_D1_6mm_P7_62mm_Horizontal031  label="R_Axial_DIN0204_L3.6mm_D1.6mm_P7.62mm_Horizontal031"
  Group = -> [Part__Feature084]
  Origin = -> Origin084
  Placement = pos=(171.71,-120.82,1.65) rot=(0,0,-1;1.5708rad)
FEATURE [Part::Feature] Part__Feature085  label="SOLID083"
  shape: bbox 8.285 x 1.732 x 4.666 mm, 17 faces (baked)
FEATURE [App::Part] R_Axial_DIN0204_L3_6mm_D1_6mm_P7_62mm_Horizontal032  label="R_Axial_DIN0204_L3.6mm_D1.6mm_P7.62mm_Horizontal032"
  Group = -> [Part__Feature085]
  Origin = -> Origin085
  Placement = pos=(131.11,-90.19,1.65) rot=(0,0,1;0rad)
FEATURE [Part::Feature] Part__Feature086  label="SOLID084"
  shape: bbox 8.285 x 1.732 x 4.666 mm, 17 faces (baked)
FEATURE [App::Part] R_Axial_DIN0204_L3_6mm_D1_6mm_P7_62mm_Horizontal033  label="R_Axial_DIN0204_L3.6mm_D1.6mm_P7.62mm_Horizontal033"
  Group = -> [Part__Feature086]
  Origin = -> Origin086
  Placement = pos=(193.58,-128.32,1.65) rot=(0,0,1;1.5708rad)
FEATURE [Part::Feature] Part__Feature087  label="SOLID085"
  shape: bbox 8.285 x 1.732 x 4.666 mm, 17 faces (baked)
FEATURE [App::Part] R_Axial_DIN0204_L3_6mm_D1_6mm_P7_62mm_Horizontal034  label="R_Axial_DIN0204_L3.6mm_D1.6mm_P7.62mm_Horizontal034"
  Group = -> [Part__Feature087]
  Origin = -> Origin087
  Placement = pos=(142.7,-108.2,1.65) rot=(0,0,1;0rad)
FEATURE [Part::Feature] Part__Feature088  label="SOLID086"
  shape: bbox 8.285 x 1.732 x 4.666 mm, 17 faces (baked)
FEATURE [App::Part] R_Axial_DIN0204_L3_6mm_D1_6mm_P7_62mm_Horizontal035  label="R_Axial_DIN0204_L3.6mm_D1.6mm_P7.62mm_Horizontal035"
  Group = -> [Part__Feature088]
  Origin = -> Origin088
  Placement = pos=(155.7,-111,1.65) rot=(0,0,-1;1.5708rad)
FEATURE [Part::Feature] Part__Feature089  label="SOLID087"
  shape: bbox 8.285 x 1.732 x 4.666 mm, 17 faces (baked)
FEATURE [App::Part] R_Axial_DIN0204_L3_6mm_D1_6mm_P7_62mm_Horizontal036  label="R_Axial_DIN0204_L3.6mm_D1.6mm_P7.62mm_Horizontal036"
  Group = -> [Part__Feature089]
  Origin = -> Origin089
  Placement = pos=(153.3,-118.6,1.65) rot=(0,0,1;1.5708rad)
FEATURE [Part::Feature] Part__Feature090  label="SOLID088"
  shape: bbox 8.285 x 1.732 x 4.666 mm, 17 faces (baked)
FEATURE [App::Part] R_Axial_DIN0204_L3_6mm_D1_6mm_P7_62mm_Horizontal037  label="R_Axial_DIN0204_L3.6mm_D1.6mm_P7.62mm_Horizontal037"
  Group = -> [Part__Feature090]
  Origin = -> Origin090
  Placement = pos=(150.9,-111,1.65) rot=(0,0,-1;1.5708rad)
FEATURE [Part::Feature] Part__Feature091  label="SOLID089"
  shape: bbox 8.285 x 1.732 x 4.666 mm, 17 faces (baked)
FEATURE [App::Part] R_Axial_DIN0204_L3_6mm_D1_6mm_P7_62mm_Horizontal038  label="R_Axial_DIN0204_L3.6mm_D1.6mm_P7.62mm_Horizontal038"
  Group = -> [Part__Feature091]
  Origin = -> Origin091
  Placement = pos=(189.1,-114.6,1.65) rot=(0,0,1;1.5708rad)
FEATURE [Part::Feature] Part__Feature092  label="SOLID090"
  shape: bbox 8.285 x 1.732 x 4.666 mm, 17 faces (baked)
FEATURE [App::Part] R_Axial_DIN0204_L3_6mm_D1_6mm_P7_62mm_Horizontal039  label="R_Axial_DIN0204_L3.6mm_D1.6mm_P7.62mm_Horizontal039"
  Group = -> [Part__Feature092]
  Origin = -> Origin092
  Placement = pos=(198.3,-110.2,1.65) rot=(0,0,1;0rad)
FEATURE [Part::Feature] Part__Feature093  label="SOLID091"
  shape: bbox 8.285 x 1.732 x 4.666 mm, 17 faces (baked)
FEATURE [App::Part] R_Axial_DIN0204_L3_6mm_D1_6mm_P7_62mm_Horizontal040  label="R_Axial_DIN0204_L3.6mm_D1.6mm_P7.62mm_Horizontal040"
  Group = -> [Part__Feature093]
  Origin = -> Origin093
  Placement = pos=(183.7,-114.6,1.65) rot=(0,0,1;1.5708rad)
FEATURE [Part::Feature] Part__Feature094  label="SOLID092"
  shape: bbox 8.285 x 1.732 x 4.666 mm, 17 faces (baked)
FEATURE [App::Part] R_Axial_DIN0204_L3_6mm_D1_6mm_P7_62mm_Horizontal041  label="R_Axial_DIN0204_L3.6mm_D1.6mm_P7.62mm_Horizontal041"
  Group = -> [Part__Feature094]
  Origin = -> Origin094
  Placement = pos=(186.4,-106.98,1.65) rot=(0,0,-1;1.5708rad)
FEATURE [Part::Feature] Part__Feature095  label="SOLID093"
  shape: bbox 8.285 x 1.732 x 4.666 mm, 17 faces (baked)
FEATURE [App::Part] R_Axial_DIN0204_L3_6mm_D1_6mm_P7_62mm_Horizontal042  label="R_Axial_DIN0204_L3.6mm_D1.6mm_P7.62mm_Horizontal042"
  Group = -> [Part__Feature095]
  Origin = -> Origin095
  Placement = pos=(198.3,-105,1.65) rot=(0,0,1;0rad)
FEATURE [Part::Feature] Part__Feature096  label="SOLID094"
  shape: bbox 8.285 x 1.732 x 4.666 mm, 17 faces (baked)
FEATURE [App::Part] R_Axial_DIN0204_L3_6mm_D1_6mm_P7_62mm_Horizontal043  label="R_Axial_DIN0204_L3.6mm_D1.6mm_P7.62mm_Horizontal043"
  Group = -> [Part__Feature096]
  Origin = -> Origin096
  Placement = pos=(205.9,-107.6,1.65) rot=(0,0,1;3.14159rad)
FEATURE [Part::Feature] Part__Feature097  label="SOLID095"
  shape: bbox 8.285 x 1.732 x 4.666 mm, 17 faces (baked)
FEATURE [App::Part] R_Axial_DIN0204_L3_6mm_D1_6mm_P7_62mm_Horizontal044  label="R_Axial_DIN0204_L3.6mm_D1.6mm_P7.62mm_Horizontal044"
  Group = -> [Part__Feature097]
  Origin = -> Origin097
  Placement = pos=(183.7,-103.2,1.65) rot=(0,0,1;1.5708rad)
FEATURE [Part::Feature] Part__Feature098  label="SOLID096"
  shape: bbox 8.285 x 1.732 x 4.666 mm, 17 faces (baked)
FEATURE [App::Part] R_Axial_DIN0204_L3_6mm_D1_6mm_P7_62mm_Horizontal045  label="R_Axial_DIN0204_L3.6mm_D1.6mm_P7.62mm_Horizontal045"
  Group = -> [Part__Feature098]
  Origin = -> Origin098
  Placement = pos=(191.3,-87,1.65) rot=(0,0,1;3.14159rad)
FEATURE [Part::Feature] Part__Feature099  label="SOLID097"
  shape: bbox 8.285 x 1.732 x 4.666 mm, 17 faces (baked)
FEATURE [App::Part] R_Axial_DIN0204_L3_6mm_D1_6mm_P7_62mm_Horizontal046  label="R_Axial_DIN0204_L3.6mm_D1.6mm_P7.62mm_Horizontal046"
  Group = -> [Part__Feature099]
  Origin = -> Origin099
  Placement = pos=(183.7,-89.6,1.65) rot=(0,0,1;0rad)
FEATURE [Part::Feature] Part__Feature100  label="SOLID098"
  shape: bbox 8.285 x 1.732 x 4.666 mm, 17 faces (baked)
FEATURE [App::Part] R_Axial_DIN0204_L3_6mm_D1_6mm_P7_62mm_Horizontal047  label="R_Axial_DIN0204_L3.6mm_D1.6mm_P7.62mm_Horizontal047"
  Group = -> [Part__Feature100]
  Origin = -> Origin100
  Placement = pos=(183.7,-92.2,1.65) rot=(0,0,1;0rad)
FEATURE [Part::Feature] Part__Feature101  label="SOLID099"
  shape: bbox 8.285 x 1.732 x 4.666 mm, 17 faces (baked)
FEATURE [App::Part] R_Axial_DIN0204_L3_6mm_D1_6mm_P7_62mm_Horizontal048  label="R_Axial_DIN0204_L3.6mm_D1.6mm_P7.62mm_Horizontal048"
  Group = -> [Part__Feature101]
  Origin = -> Origin101
  Placement = pos=(210.1,-111,1.65) rot=(0,0,1;0rad)
FEATURE [Part::Feature] Part__Feature102  label="SOLID100"
  shape: bbox 8.285 x 1.732 x 4.666 mm, 17 faces (baked)
FEATURE [App::Part] R_Axial_DIN0204_L3_6mm_D1_6mm_P7_62mm_Horizontal049  label="R_Axial_DIN0204_L3.6mm_D1.6mm_P7.62mm_Horizontal049"
  Group = -> [Part__Feature102]
  Origin = -> Origin102
  Placement = pos=(210.1,-105,1.65) rot=(0,0,1;0rad)
FEATURE [Part::Feature] Part__Feature103  label="SOLID101"
  shape: bbox 8.285 x 1.732 x 4.666 mm, 17 faces (baked)
FEATURE [App::Part] R_Axial_DIN0204_L3_6mm_D1_6mm_P7_62mm_Horizontal050  label="R_Axial_DIN0204_L3.6mm_D1.6mm_P7.62mm_Horizontal050"
  Group = -> [Part__Feature103]
  Origin = -> Origin103
  Placement = pos=(221.3,-105,1.65) rot=(0,0,-1;1.5708rad)
FEATURE [Part::Feature] Part__Feature104  label="SOLID102"
  shape: bbox 8.285 x 1.732 x 4.666 mm, 17 faces (baked)
FEATURE [App::Part] R_Axial_DIN0204_L3_6mm_D1_6mm_P7_62mm_Horizontal051  label="R_Axial_DIN0204_L3.6mm_D1.6mm_P7.62mm_Horizontal051"
  Group = -> [Part__Feature104]
  Origin = -> Origin104
  Placement = pos=(223.8,-105,1.65) rot=(0,0,-1;1.5708rad)
FEATURE [Part::Feature] Part__Feature105  label="SOLID103"
  shape: bbox 8.285 x 1.732 x 4.666 mm, 17 faces (baked)
FEATURE [App::Part] R_Axial_DIN0204_L3_6mm_D1_6mm_P7_62mm_Horizontal052  label="R_Axial_DIN0204_L3.6mm_D1.6mm_P7.62mm_Horizontal052"
  Group = -> [Part__Feature105]
  Origin = -> Origin105
  Placement = pos=(226.3,-112.6,1.65) rot=(0,0,1;1.5708rad)
FEATURE [Part::Feature] Part__Feature106  label="SOLID104"
  shape: bbox 12.5 x 12.5 x 13.85 mm, 27 faces (baked)
FEATURE [App::Part] L_Radial_D12_5mm_P7_00mm_Fastron_09HCP001  label="L_Radial_D12.5mm_P7.00mm_Fastron_09HCP001"
  Group = -> [Part__Feature106]
  Origin = -> Origin106
  Placement = pos=(236.9,-113.7,1.65) rot=(0,0,1;1.5708rad)
FEATURE [Part::Feature] Part__Feature107  label="SOLID105"
  shape: bbox 12.5 x 12.5 x 13.85 mm, 27 faces (baked)
FEATURE [App::Part] L_Radial_D12_5mm_P7_00mm_Fastron_09HCP002  label="L_Radial_D12.5mm_P7.00mm_Fastron_09HCP002"
  Group = -> [Part__Feature107]
  Origin = -> Origin107
  Placement = pos=(236.9,-99.5,1.65) rot=(0,0,1;1.5708rad)
FEATURE [Part::Feature] Part__Feature108  label="SOLID106"
  shape: bbox 12.5 x 12.5 x 13.85 mm, 27 faces (baked)
FEATURE [App::Part] L_Radial_D12_5mm_P7_00mm_Fastron_09HCP003  label="L_Radial_D12.5mm_P7.00mm_Fastron_09HCP003"
  Group = -> [Part__Feature108]
  Origin = -> Origin108
  Placement = pos=(250.9,-106.7,1.65) rot=(0,0,-1;1.5708rad)
FEATURE [Part::Feature] Part__Feature109  label="SOLID107"
  shape: bbox 16.36 x 5 x 8.1 mm, 35 faces (baked)
FEATURE [App::Part] L_Axial_L12_0mm_D5_0mm_P15_24mm_Horizontal_Fastron_MISC002  label="L_Axial_L12.0mm_D5.0mm_P15.24mm_Horizontal_Fastron_MISC002"
  Group = -> [Part__Feature109]
  Origin = -> Origin109
  Placement = pos=(167.5,-102.6,1.65) rot=(0,0,1;1.5708rad)
FEATURE [Part::Feature] Part__Feature110  label="SOLID108"
  shape: bbox 12.5 x 12.5 x 13.85 mm, 27 faces (baked)
FEATURE [App::Part] L_Radial_D12_5mm_P7_00mm_Fastron_09HCP004  label="L_Radial_D12.5mm_P7.00mm_Fastron_09HCP004"
  Group = -> [Part__Feature110]
  Origin = -> Origin110
  Placement = pos=(236.9,-85.3,1.65) rot=(0,0,1;1.5708rad)
FEATURE [Part::Feature] Part__Feature111  label="SOLID109"
  shape: bbox 16.36 x 5 x 8.1 mm, 35 faces (baked)
FEATURE [App::Part] L_Axial_L12_0mm_D5_0mm_P15_24mm_Horizontal_Fastron_MISC003  label="L_Axial_L12.0mm_D5.0mm_P15.24mm_Horizontal_Fastron_MISC003"
  Group = -> [Part__Feature111]
  Origin = -> Origin111
  Placement = pos=(210.7,-88.4,1.65) rot=(0,0,1;0rad)
FEATURE [Part::Feature] Part__Feature112  label="SOLID110"
  shape: bbox 7.2 x 2.5 x 10.9 mm, 22 faces (baked)
FEATURE [App::Part] C_Rect_L7_2mm_W2_5mm_P5_00mm_FKS2_FKP2_MKS2_MKP2016  label="C_Rect_L7.2mm_W2.5mm_P5.00mm_FKS2_FKP2_MKS2_MKP018"
  Group = -> [Part__Feature112]
  Origin = -> Origin112
  Placement = pos=(148.1,-111.6,1.65) rot=(0,0,1;3.14159rad)
FEATURE [Part::Feature] Part__Feature113  label="SOLID111"
  shape: bbox 7.2 x 2.5 x 10.9 mm, 22 faces (baked)
FEATURE [App::Part] C_Rect_L7_2mm_W2_5mm_P5_00mm_FKS2_FKP2_MKS2_MKP2017  label="C_Rect_L7.2mm_W2.5mm_P5.00mm_FKS2_FKP2_MKS2_MKP019"
  Group = -> [Part__Feature113]
  Origin = -> Origin113
  Placement = pos=(152.9,-108.2,1.65) rot=(0,0,1;0rad)
FEATURE [Part::Feature] Part__Feature114  label="SOLID112"
  shape: bbox 6 x 2.5 x 8.1 mm, 12 faces (baked)
FEATURE [App::Part] C_Disc_D6_0mm_W2_5mm_P5_00mm004  label="C_Disc_D6.0mm_W2.5mm_P5.00mm004"
  Group = -> [Part__Feature114]
  Origin = -> Origin114
  Placement = pos=(192.7,-113.6,1.65) rot=(0,0,1;1.5708rad)
FEATURE [Part::Feature] Part__Feature115  label="SOLID113"
  shape: bbox 6 x 2.5 x 8.1 mm, 12 faces (baked)
FEATURE [App::Part] C_Disc_D6_0mm_W2_5mm_P5_00mm005  label="C_Disc_D6.0mm_W2.5mm_P5.00mm005"
  Group = -> [Part__Feature115]
  Origin = -> Origin115
  Placement = pos=(204.9,-114,1.65) rot=(0,0,1;3.14159rad)
FEATURE [Part::Feature] Part__Feature116  label="SOLID114"
  shape: bbox 6 x 2.5 x 8.1 mm, 12 faces (baked)
FEATURE [App::Part] C_Disc_D6_0mm_W2_5mm_P5_00mm006  label="C_Disc_D6.0mm_W2.5mm_P5.00mm006"
  Group = -> [Part__Feature116]
  Origin = -> Origin116
  Placement = pos=(180.5,-107.6,1.65) rot=(0,0,1;3.14159rad)
FEATURE [Part::Feature] Part__Feature117  label="SOLID115"
  shape: bbox 6 x 2.5 x 8.1 mm, 12 faces (baked)
FEATURE [App::Part] C_Disc_D6_0mm_W2_5mm_P5_00mm007  label="C_Disc_D6.0mm_W2.5mm_P5.00mm007"
  Group = -> [Part__Feature117]
  Origin = -> Origin117
  Placement = pos=(205.3,-101.8,1.65) rot=(0,0,1;1.5708rad)
FEATURE [Part::Feature] Part__Feature118  label="SOLID116"
  shape: bbox 7.2 x 2.5 x 10.9 mm, 22 faces (baked)
FEATURE [App::Part] C_Rect_L7_2mm_W2_5mm_P5_00mm_FKS2_FKP2_MKS2_MKP2018  label="C_Rect_L7.2mm_W2.5mm_P5.00mm_FKS2_FKP2_MKS2_MKP020"
  Group = -> [Part__Feature118]
  Origin = -> Origin118
  Placement = pos=(190.7,-102,1.65) rot=(0,0,1;1.5708rad)
FEATURE [Part::Feature] Part__Feature119  label="SOLID117"
  shape: bbox 7.2 x 2.5 x 10.9 mm, 22 faces (baked)
FEATURE [App::Part] C_Rect_L7_2mm_W2_5mm_P5_00mm_FKS2_FKP2_MKS2_MKP2019  label="C_Rect_L7.2mm_W2.5mm_P5.00mm_FKS2_FKP2_MKS2_MKP021"
  Group = -> [Part__Feature119]
  Origin = -> Origin119
  Placement = pos=(186.9,-102,1.65) rot=(0,0,1;1.5708rad)
FEATURE [Part::Feature] Part__Feature120  label="SOLID118"
  shape: bbox 6 x 2.5 x 8.1 mm, 12 faces (baked)
FEATURE [App::Part] C_Disc_D6_0mm_W2_5mm_P5_00mm008  label="C_Disc_D6.0mm_W2.5mm_P5.00mm008"
  Group = -> [Part__Feature120]
  Origin = -> Origin120
  Placement = pos=(172.4,-103.1,1.65) rot=(0,0,1;1.5708rad)
FEATURE [Part::Feature] Part__Feature121  label="SOLID119"
  shape: bbox 7.2 x 2.5 x 10.9 mm, 22 faces (baked)
FEATURE [App::Part] C_Rect_L7_2mm_W2_5mm_P5_00mm_FKS2_FKP2_MKS2_MKP2020  label="C_Rect_L7.2mm_W2.5mm_P5.00mm_FKS2_FKP2_MKS2_MKP022"
  Group = -> [Part__Feature121]
  Origin = -> Origin121
  Placement = pos=(211.6,-114,1.65) rot=(0,0,1;0rad)
FEATURE [Part::Feature] Part__Feature122  label="SOLID120"
  shape: bbox 7.2 x 2.5 x 10.9 mm, 22 faces (baked)
FEATURE [App::Part] C_Rect_L7_2mm_W2_5mm_P5_00mm_FKS2_FKP2_MKS2_MKP2021  label="C_Rect_L7.2mm_W2.5mm_P5.00mm_FKS2_FKP2_MKS2_MKP023"
  Group = -> [Part__Feature122]
  Origin = -> Origin122
  Placement = pos=(211.6,-108,1.65) rot=(0,0,1;0rad)
FEATURE [Part::Feature] Part__Feature123  label="SOLID121"
  shape: bbox 6 x 2.5 x 8.1 mm, 12 faces (baked)
FEATURE [App::Part] C_Disc_D6_0mm_W2_5mm_P5_00mm009  label="C_Disc_D6.0mm_W2.5mm_P5.00mm009"
  Group = -> [Part__Feature123]
  Origin = -> Origin123
  Placement = pos=(215.3,-93.1,1.65) rot=(0,0,1;3.14159rad)
FEATURE [Part::Feature] Part__Feature124  label="SOLID122"
  shape: bbox 6 x 2.5 x 8.1 mm, 12 faces (baked)
FEATURE [App::Part] C_Disc_D6_0mm_W2_5mm_P5_00mm010  label="C_Disc_D6.0mm_W2.5mm_P5.00mm010"
  Group = -> [Part__Feature124]
  Origin = -> Origin124
  Placement = pos=(221.3,-93.15,1.65) rot=(0,0,1;0rad)
FEATURE [Part::Feature] Part__Feature125  label="COMPOUND002"
  shape: bbox 214 x 69.7 x 1.6 mm, 444 faces (baked)
FEATURE [App::Part] Open_CASCADE_STEP_translator_6_9_1  label="Open CASCADE STEP translator 6.9 1"
  Group = -> [CP_Radial_D16_0mm_P7_50mm,CP_Radial_D16_0mm_P7_50mm001,R_Axial_DIN0204_L3_6mm_D1_6mm_P7_62mm_Horizontal,D_DO_34_SOD68_P7_62mm_Horizontal,D_DO_34_SOD68_P7_62mm_Horizontal001,D_DO_34_SOD68_P7_62mm_Horizontal002,PinHeader_1x04_P2_54mm_Vertical,R_Axial_DIN0204_L3_6mm_D1_6mm_P7_62mm_Horizontal001,R_Axial_DIN0204_L3_6mm_D1_6mm_P7_62mm_Horizontal002,DIP_8_W7_62mm,DIP_14_W7_62mm,+115 more]
  Origin = -> Origin125
  Placement = pos=(-39,135,4) rot=(0,0,1;0rad)
FEATURE [Part::Cylinder] Cylinder001
  Angle = 360
  AttacherType = Attacher::AttachEngine3D
  Height = 6.3
  Placement = pos=(6,9.5,0) rot=(0,0,1;0rad)
  Radius = 4
FEATURE [Part::Cylinder] Cylinder002  label="ScrewHole001"
  Angle = 360
  AttacherType = Attacher::AttachEngine3D
  Height = 7
  Placement = pos=(6,71.2,0) rot=(0,0,1;0rad)
  Radius = 1.25
FEATURE [Part::Cylinder] Cylinder003  label="ScrewHole002"
  Angle = 360
  AttacherType = Attacher::AttachEngine3D
  Height = 7
  Placement = pos=(214,71.2,0) rot=(0,0,1;0rad)
  Radius = 1.25
FEATURE [Part::Cylinder] Cylinder004  label="ScrewHole003"
  Angle = 360
  AttacherType = Attacher::AttachEngine3D
  Height = 7
  Placement = pos=(214,9.5,0) rot=(0,0,1;0rad)
  Radius = 1.25
FEATURE [Part::Cylinder] Cylinder005
  Angle = 360
  AttacherType = Attacher::AttachEngine3D
  Height = 6.3
  Placement = pos=(6,71.2,0) rot=(0,0,1;0rad)
  Radius = 4
FEATURE [Part::Cylinder] Cylinder006
  Angle = 360
  AttacherType = Attacher::AttachEngine3D
  Height = 6.3
  Placement = pos=(214,71.2,0) rot=(0,0,1;0rad)
  Radius = 4
FEATURE [Part::Cylinder] Cylinder007
  Angle = 360
  AttacherType = Attacher::AttachEngine3D
  Height = 6.3
  Placement = pos=(214,9.5,0) rot=(0,0,1;0rad)
  Radius = 4
FEATURE [Part::Box] Box002  label="BigPocket"
  AttacherType = Attacher::AttachEngine3D
  Height = 3
  Length = 190
  Placement = pos=(15,6,1) rot=(0,0,1;0rad)
  Width = 68
FEATURE [Part::Box] Box003  label="Reinforce"
  AttacherType = Attacher::AttachEngine3D
  Height = 2
  Length = 2
  Placement = pos=(111,6,1) rot=(0,0,1;0rad)
  Width = 68
FEATURE [Part::MultiFuse] Fusion  label="BaseHoles"
  Shapes = -> [Box002,Cylinder004,Cylinder002,Cylinder003,Cylinder]
FEATURE [Part::MultiFuse] Fusion001  label="BaseFusion"
  Shapes = -> [Cylinder007,Cylinder005,Cylinder006,Cylinder001,Box]
FEATURE [Part::Cut] Cut  label="BaseSubstraction"
  Base = -> Fusion001
  Tool = -> Fusion
FEATURE [Part::Box] Box004  label="Reinforce001"
  AttacherType = Attacher::AttachEngine3D
  Height = 2
  Length = 190
  Placement = pos=(15,39,1) rot=(0,0,1;0rad)
  Width = 2
FEATURE [Part::Box] Box005  label="Cube002"
  AttacherType = Attacher::AttachEngine3D
  Height = 40
  Length = 2
  Width = 80
FEATURE [Part::Box] Box006  label="Cube"
  AttacherType = Attacher::AttachEngine3D
  Height = 20
  Length = 2
  Placement = pos=(0,34.2,35) rot=(0,0,1;0rad)
  Width = 10
FEATURE [Part::Fillet] Fillet
  Base = -> Box006
  Edges = 2 edges r=4.4: [Edge9,Edge11]
FEATURE [Part::Cylinder] Cylinder008  label="Cylinder"
  Angle = 360
  AttacherType = Attacher::AttachEngine3D
  Height = 10
  Placement = pos=(0,48,51) rot=(0,1,0;1.5708rad)
  Radius = 1.25
FEATURE [Part::MultiFuse] Fusion003
  Placement = pos=(0,1,-15) rot=(0,0,1;0rad)
  Shapes = -> [Cylinder008,Fillet]
FEATURE [Part::Box] Box009  label="Cube005"
  AttacherType = Attacher::AttachEngine3D
  Height = 6
  Length = 13
  Placement = pos=(2,29,0) rot=(0,0,1;0rad)
  Width = 6.8
FEATURE [Part::Fillet] Fillet002
  Base = -> Box009
  Edges = 2 edges r=2: [Edge10,Edge12]
  Placement = pos=(0,-2,0) rot=(0,0,1;0rad)
FEATURE [Part::Cylinder] Cylinder010  label="Cylinder009"
  Angle = 360
  AttacherType = Attacher::AttachEngine3D
  Height = 20
  Placement = pos=(0,30.5,4) rot=(0,1,0;1.5708rad)
  Radius = 1.25
FEATURE [Part::Box] Box001  label="Cube001"
  AttacherType = Attacher::AttachEngine3D
  Height = 2
  Length = 220
  Placement = pos=(0,82,0) rot=(0,0,1;0rad)
  Width = 80
FEATURE [Part::Cylinder] Cylinder011  label="Cylinder010"
  Angle = 360
  AttacherType = Attacher::AttachEngine3D
  Height = 20
  Placement = pos=(204,30.5,4) rot=(0,1,0;1.5708rad)
  Radius = 1.25
FEATURE [Part::MultiFuse] Fusion005
  Shapes = -> [Cylinder011,Cylinder010]
FEATURE [Part::Box] Box010  label="Cube006"
  AttacherType = Attacher::AttachEngine3D
  Height = 35
  Length = 224
  Placement = pos=(0,82,17) rot=(0,0,1;0rad)
  Width = 2
FEATURE [Part::Cylinder] Cylinder012  label="FootBase"
  Angle = 360
  AttacherType = Attacher::AttachEngine3D
  Height = 5
  Placement = pos=(9,9.5,-5) rot=(0,0,1;0rad)
  Radius = 9.5
FEATURE [Part::Cylinder] Cylinder013  label="FootBase001"
  Angle = 360
  AttacherType = Attacher::AttachEngine3D
  Height = 5
  Placement = pos=(9,9.5,-4) rot=(0,0,1;0rad)
  Radius = 1.1
FEATURE [Part::Cut] Cut001002  label="Footsub"
  Base = -> Cylinder012
  Placement = pos=(0,-22,0) rot=(0,0,1;0rad)
  Tool = -> Cylinder013
FEATURE [Mesh::Feature] Mesh  label="Bottom (Meshed)"
  Placement = pos=(0,-118,0) rot=(0,0,1;0rad)
FEATURE [Part::Cylinder] Cylinder014  label="Cylinder011"
  Angle = 360
  AttacherType = Attacher::AttachEngine3D
  Height = 6
  Placement = pos=(-5,10.6,0) rot=(0,0,1;0rad)
  Radius = 1.6
FEATURE [Part::Cylinder] Cylinder018  label="Cylinder015"
  Angle = 360
  AttacherType = Attacher::AttachEngine3D
  Height = 2.2
  Placement = pos=(-5,10.6,0) rot=(0,0,1;0rad)
  Radius = 4
FEATURE [Part::Cylinder] Cylinder019  label="Cylinder016"
  Angle = 360
  AttacherType = Attacher::AttachEngine3D
  Height = 10
  Placement = pos=(89,119,0) rot=(0,0,1;0rad)
  Radius = 2
FEATURE [Part::Cylinder] Cylinder020  label="Cylinder017"
  Angle = 360
  AttacherType = Attacher::AttachEngine3D
  Height = 10
  Placement = pos=(89,112,0) rot=(0,0,1;0rad)
  Radius = 2
FEATURE [Part::Cylinder] Cylinder021  label="Cylinder018"
  Angle = 360
  AttacherType = Attacher::AttachEngine3D
  Height = 10
  Placement = pos=(89,126,0) rot=(0,0,1;0rad)
  Radius = 2
FEATURE [Part::Cylinder] Cylinder022  label="Cylinder019"
  Angle = 360
  AttacherType = Attacher::AttachEngine3D
  Height = 10
  Placement = pos=(89,133,0) rot=(0,0,1;0rad)
  Radius = 2
FEATURE [Part::Cylinder] Cylinder023  label="Cylinder020"
  Angle = 360
  AttacherType = Attacher::AttachEngine3D
  Height = 10
  Placement = pos=(96,133,0) rot=(0,0,1;0rad)
  Radius = 2
FEATURE [Part::Cylinder] Cylinder024  label="Cylinder021"
  Angle = 360
  AttacherType = Attacher::AttachEngine3D
  Height = 10
  Placement = pos=(103,133,0) rot=(0,0,1;0rad)
  Radius = 2
FEATURE [Part::Cylinder] Cylinder025  label="Cylinder022"
  Angle = 360
  AttacherType = Attacher::AttachEngine3D
  Height = 10
  Placement = pos=(110,133,0) rot=(0,0,1;0rad)
  Radius = 2
FEATURE [Part::Cylinder] Cylinder026  label="Cylinder023"
  Angle = 360
  AttacherType = Attacher::AttachEngine3D
  Height = 10
  Placement = pos=(117,133,0) rot=(0,0,1;0rad)
  Radius = 2
FEATURE [Part::Cylinder] Cylinder027  label="Cylinder024"
  Angle = 360
  AttacherType = Attacher::AttachEngine3D
  Height = 10
  Placement = pos=(124,133,0) rot=(0,0,1;0rad)
  Radius = 2
FEATURE [Part::Cylinder] Cylinder028  label="Cylinder025"
  Angle = 360
  AttacherType = Attacher::AttachEngine3D
  Height = 10
  Placement = pos=(131,133,0) rot=(0,0,1;0rad)
  Radius = 2
FEATURE [Part::Cylinder] Cylinder029  label="Cylinder030"
  Angle = 360
  AttacherType = Attacher::AttachEngine3D
  Height = 10
  Placement = pos=(131,126,0) rot=(0,0,1;0rad)
  Radius = 2
FEATURE [Part::Cylinder] Cylinder030  label="Cylinder031"
  Angle = 360
  AttacherType = Attacher::AttachEngine3D
  Height = 10
  Placement = pos=(110,126,0) rot=(0,0,1;0rad)
  Radius = 2
FEATURE [Part::Cylinder] Cylinder031  label="Cylinder034"
  Angle = 360
  AttacherType = Attacher::AttachEngine3D
  Height = 10
  Placement = pos=(117,126,0) rot=(0,0,1;0rad)
  Radius = 2
FEATURE [Part::Cylinder] Cylinder032  label="Cylinder033"
  Angle = 360
  AttacherType = Attacher::AttachEngine3D
  Height = 10
  Placement = pos=(124,126,0) rot=(0,0,1;0rad)
  Radius = 2
FEATURE [Part::Cylinder] Cylinder033  label="Cylinder035"
  Angle = 360
  AttacherType = Attacher::AttachEngine3D
  Height = 10
  Placement = pos=(103,126,0) rot=(0,0,1;0rad)
  Radius = 2
FEATURE [Part::Cylinder] Cylinder034  label="Cylinder036"
  Angle = 360
  AttacherType = Attacher::AttachEngine3D
  Height = 10
  Placement = pos=(96,126,0) rot=(0,0,1;0rad)
  Radius = 2
FEATURE [Part::Cylinder] Cylinder035  label="Cylinder037"
  Angle = 360
  AttacherType = Attacher::AttachEngine3D
  Height = 10
  Placement = pos=(96,119,0) rot=(0,0,1;0rad)
  Radius = 2
FEATURE [Part::Cylinder] Cylinder036  label="Cylinder039"
  Angle = 360
  AttacherType = Attacher::AttachEngine3D
  Height = 10
  Placement = pos=(96,112,0) rot=(0,0,1;0rad)
  Radius = 2
FEATURE [Part::Cylinder] Cylinder037  label="Cylinder040"
  Angle = 360
  AttacherType = Attacher::AttachEngine3D
  Height = 10
  Placement = pos=(103,119,0) rot=(0,0,1;0rad)
  Radius = 2
FEATURE [Part::Cylinder] Cylinder038  label="Cylinder041"
  Angle = 360
  AttacherType = Attacher::AttachEngine3D
  Height = 10
  Placement = pos=(124,119,0) rot=(0,0,1;0rad)
  Radius = 2
FEATURE [Part::Cylinder] Cylinder039  label="Cylinder042"
  Angle = 360
  AttacherType = Attacher::AttachEngine3D
  Height = 10
  Placement = pos=(110,119,0) rot=(0,0,1;0rad)
  Radius = 2
FEATURE [Part::Cylinder] Cylinder040  label="Cylinder043"
  Angle = 360
  AttacherType = Attacher::AttachEngine3D
  Height = 10
  Placement = pos=(117,119,0) rot=(0,0,1;0rad)
  Radius = 2
FEATURE [Part::Cylinder] Cylinder041  label="Cylinder044"
  Angle = 360
  AttacherType = Attacher::AttachEngine3D
  Height = 10
  Placement = pos=(131,119,0) rot=(0,0,1;0rad)
  Radius = 2
FEATURE [Part::Cylinder] Cylinder042  label="Cylinder045"
  Angle = 360
  AttacherType = Attacher::AttachEngine3D
  Height = 10
  Placement = pos=(103,112,0) rot=(0,0,1;0rad)
  Radius = 2
FEATURE [Part::Cylinder] Cylinder043  label="Cylinder046"
  Angle = 360
  AttacherType = Attacher::AttachEngine3D
  Height = 10
  Placement = pos=(110,112,0) rot=(0,0,1;0rad)
  Radius = 2
FEATURE [Part::Cylinder] Cylinder044  label="Cylinder047"
  Angle = 360
  AttacherType = Attacher::AttachEngine3D
  Height = 10
  Placement = pos=(117,112,0) rot=(0,0,1;0rad)
  Radius = 2
FEATURE [Part::Cylinder] Cylinder045  label="Cylinder048"
  Angle = 360
  AttacherType = Attacher::AttachEngine3D
  Height = 10
  Placement = pos=(124,112,0) rot=(0,0,1;0rad)
  Radius = 2
FEATURE [Part::Cylinder] Cylinder046  label="Cylinder049"
  Angle = 360
  AttacherType = Attacher::AttachEngine3D
  Height = 10
  Placement = pos=(131,112,0) rot=(0,0,1;0rad)
  Radius = 2
FEATURE [Part::Box] Box013  label="Cube009"
  AttacherType = Attacher::AttachEngine3D
  Height = 2
  Length = 66
  Placement = pos=(6,89,1) rot=(0,0,1;0rad)
  Width = 66
FEATURE [Part::Box] Box014  label="Reinforce002"
  AttacherType = Attacher::AttachEngine3D
  Height = 1.5
  Length = 95
  Placement = pos=(6,87,0.5) rot=(0,0,1;0.785398rad)
  Width = 3
FEATURE [Part::Box] Box015  label="Reinforce003"
  AttacherType = Attacher::AttachEngine3D
  Height = 1.5
  Length = 95
  Placement = pos=(4,155,0.5) rot=(0,0,-1;0.785398rad)
  Width = 3
FEATURE [Part::Box] Box016  label="Cube012"
  AttacherType = Attacher::AttachEngine3D
  Height = 2
  Length = 66
  Placement = pos=(148,89,1) rot=(0,0,1;0rad)
  Width = 66
FEATURE [Part::Box] Box017  label="Cube013"
  AttacherType = Attacher::AttachEngine3D
  Height = 2
  Length = 72
  Placement = pos=(74,89,1) rot=(0,0,1;0rad)
  Width = 18
FEATURE [Part::Box] Box018  label="Cube014"
  AttacherType = Attacher::AttachEngine3D
  Height = 2
  Length = 72
  Placement = pos=(74,137,1) rot=(0,0,1;0rad)
  Width = 18
FEATURE [Part::MultiFuse] Fusion006
  Shapes = -> [Box018,Box017,Box016,Box013,Cylinder046,Cylinder043,Cylinder040,Cylinder022,Cylinder025,Cylinder020,Cylinder038,Cylinder023,Cylinder029,Cylinder019,Cylinder031,Cylinder035,Cylinder026,Cylinder032,Cylinder037,Cylinder034,Cylinder030,Cylinder028,Cylinder027,Cylinder033,Cylinder021,Cylinder036,Cylinder024,Cylinder042,Cylinder041,Cylinder039,Cylinder044,Cylinder045]
FEATURE [Part::Cut] Cut001004  label="Lid"
  Base = -> Box001
  Tool = -> Fusion006
FEATURE [Part::Box] Box019  label="Reinforce005"
  AttacherType = Attacher::AttachEngine3D
  Height = 1.5
  Length = 95
  Placement = pos=(146,155,0.5) rot=(0,0,-1;0.785398rad)
  Width = 3
FEATURE [Part::Box] Box020  label="Reinforce004"
  AttacherType = Attacher::AttachEngine3D
  Height = 1.5
  Length = 95
  Placement = pos=(148,87,0.5) rot=(0,0,1;0.785398rad)
  Width = 3
FEATURE [Part::Cut] Cut001005  label="washer"
  Base = -> Cylinder018
  Tool = -> Cylinder014
FEATURE [Mesh::Feature] Mesh003  label="washer (Meshed)"
  Placement = pos=(0,-11,0) rot=(0,0,1;0rad)
FEATURE [Part::Fillet] Fillet002003  label="Foot"
  Base = -> Cut001002
  Edges = 2 edges r=1.2: [Edge1,Edge3]
FEATURE [Mesh::Feature] Mesh004  label="Foot (Meshed)"
  Placement = pos=(0,-24,0) rot=(0,0,1;0rad)
FEATURE [Part::Box] Box021  label="Cube017"
  AttacherType = Attacher::AttachEngine3D
  Height = 6
  Length = 13
  Placement = pos=(2,29,0) rot=(0,0,1;0rad)
  Width = 6.8
FEATURE [Part::Fillet] Fillet002004
  Base = -> Box021
  Edges = 2 edges r=2: [Edge10,Edge12]
  Placement = pos=(203,-2,0) rot=(0,0,1;0rad)
FEATURE [Part::MultiFuse] Fusion008
  Shapes = -> [Fillet002004,Fillet002,Cut,Box003,Box004]
FEATURE [Part::Cut] Cut001006  label="Bottom"
  Base = -> Fusion008
  Tool = -> Fusion005
FEATURE [Part::Cut] Cut001007  label="Side"
  Base = -> Box005
  Placement = pos=(0,82,0) rot=(0,0,1;0rad)
  Tool = -> Fusion003
FEATURE [Part::Feature] Cut001007001  label="Side001"
  Placement = pos=(218,82,0) rot=(0,0,1;0rad)
  shape: bbox 2 x 80 x 40 mm, 13 faces (baked)
FEATURE [Part::MultiFuse] Fusion009
  Shapes = -> [Box014,Box015,Box019,Box020,Cut001004,Cut001007,Cut001007001]
FEATURE [Part::Fillet] Fillet002005  label="Top"
  Base = -> Fusion009
  Edges = 36 edges r=1: [Edge78,Edge91,Edge225,Edge226,Edge228,Edge230,Edge231,Edge232,Edge234,Edge237,Edge239,Edge241,Edge242,Edge243,Edge245,Edge246,Edge248,Edge249,Edge251,Edge252,Edge253,Edge255,Edge256,Edge257,Edge260,Edge261,Edge263,Edge265,Edge267,Edge268,Edge269,Edge271,Edge272,Edge274,Edge318,Edge319]
FEATURE [Mesh::Feature] Mesh006  label="Top (Meshed)"
  Placement = pos=(237,0,0) rot=(0,0,1;0rad)
FEATURE [Mesh::Feature] Mesh007  label="Bottom (Meshed)001"
  Placement = pos=(237,0,0) rot=(0,0,1;0rad)
